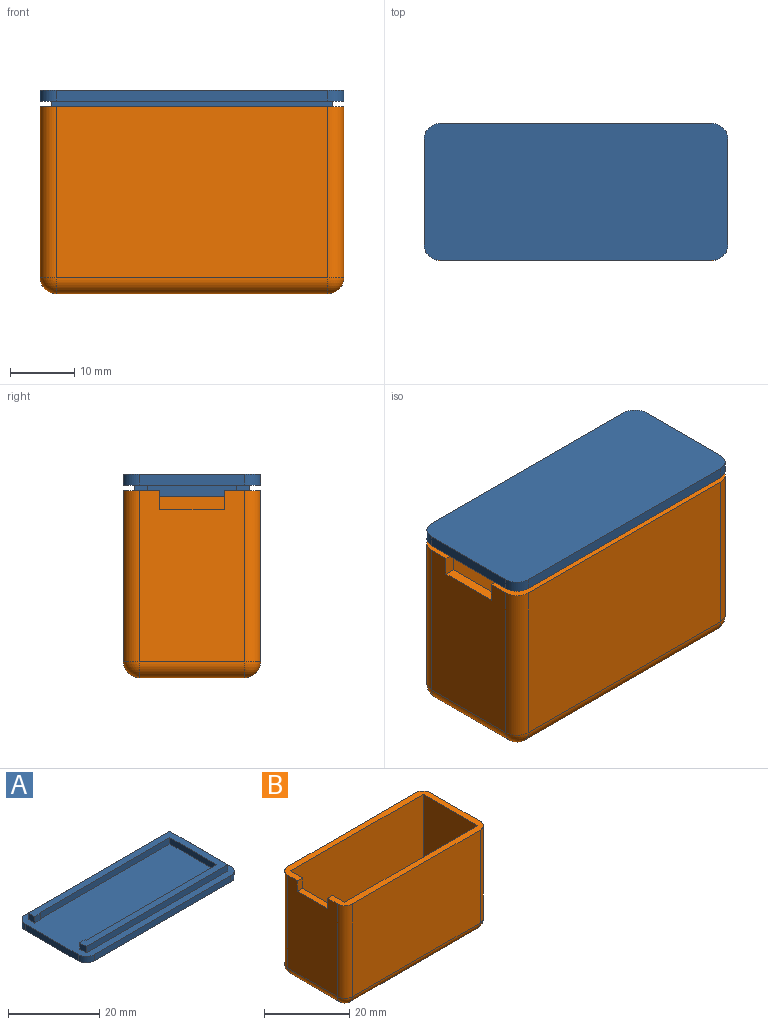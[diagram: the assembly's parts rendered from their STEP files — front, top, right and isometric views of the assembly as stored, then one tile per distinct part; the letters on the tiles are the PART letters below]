
ASSEMBLY  parts=2 mates=1
PART A: 23 faces, bbox 47.4x21.4x3.4 mm
  f0: plane 2x1.7mm, normal (-1,0,0), area 3.4mm2, adj f2,f7,f10,f18
  f1: plane 1.7x0.3mm, normal (1,0,0), area 0.5mm2, adj f2,f7,f14,f17
  f2: plane 44x18mm, normal (0,0,1), area 175.4mm2, adj f0,f1,f9,f10,f11,f12,f13,f14
  f3: plane 42.4x1.7mm, normal (0,1,0), area 72.1mm2, adj f7,f8,f19,f22
  f4: plane 16.4x1.7mm, normal (-1,0,0), area 27.9mm2, adj f7,f8,f19,f20
  f5: plane 42.4x1.7mm, normal (0,-1,0), area 72.1mm2, adj f7,f8,f20,f21
  f6: plane 16.4x1.7mm, normal (1,0,0), area 27.9mm2, adj f7,f8,f21,f22
  f7: plane 47.4x21.4mm, normal (0,0,1), area 833.6mm2, adj f0,f1,f3,f4,f5,f6,f9,f10
  f8: plane 47.4x21.4mm, normal (0,0,-1), area 1009mm2, adj f3,f4,f5,f6,f19,f20,f21,f22
  f9: plane 18x1.7mm, normal (1,0,0), area 30.6mm2, adj f2,f7,f10,f16
  f10: plane 44x1.7mm, normal (0,1,0), area 74.8mm2, adj f0,f2,f7,f9
  f11: plane 2x1.7mm, normal (-1,0,0), area 3.4mm2, adj f2,f7,f16,f17
  f12: plane 40.6x1.7mm, normal (0,-1,0), area 69mm2, adj f2,f7,f13,f15
  f13: plane 14.6x1.7mm, normal (-1,0,0), area 24.8mm2, adj f2,f7,f12,f14
  f14: plane 40.6x1.7mm, normal (0,1,0), area 69mm2, adj f1,f2,f7,f13
  f15: plane 1.7x0.3mm, normal (1,0,0), area 0.5mm2, adj f2,f7,f12,f18
  f16: plane 44x1.7mm, normal (0,-1,0), area 74.8mm2, adj f2,f7,f9,f11
  f17: plane 1.7x1.7mm, normal (0,1,0), area 2.9mm2, adj f1,f2,f7,f11
  f18: plane 1.7x1.7mm, normal (0,-1,0), area 2.9mm2, adj f0,f2,f7,f15
  f19: cylinder r=2.5mm len=2.5mm, axis (0,0,1), area 6.7mm2, adj f3,f4,f7,f8
  f20: cylinder r=2.5mm len=2.5mm, axis (0,0,-1), area 6.7mm2, adj f4,f5,f7,f8
  f21: cylinder r=2.5mm len=2.5mm, axis (0,0,1), area 6.7mm2, adj f5,f6,f7,f8
  f22: cylinder r=2.5mm len=2.5mm, axis (0,0,-1), area 6.7mm2, adj f3,f6,f7,f8
PART B: 29 faces, bbox 47.4x21.4x29.2 mm
  f0: plane 47.4x21.4mm, normal (0,0,1), area 200mm2, adj f1,f2,f3,f4,f6,f7,f8,f9
  f1: plane 26.7x16.4mm, normal (-1,0,0), area 407.9mm2, adj f0,f14,f15,f16,f22,f26,f28
  f2: plane 42.4x26.7mm, normal (0,-1,0), area 1132.1mm2, adj f0,f19,f25,f28
  f3: plane 26.7x16.4mm, normal (1,0,0), area 406.8mm2, adj f0,f11,f12,f13,f17,f19,f20
  f4: plane 42.4x26.7mm, normal (0,1,0), area 1132.1mm2, adj f0,f17,f21,f22
  f5: plane 42.4x16.4mm, normal (0,0,-1), area 695.4mm2, adj f20,f21,f25,f26
  f6: plane 27.5x18mm, normal (1,0,0), area 465mm2, adj f0,f7,f9,f10,f14,f15,f16
  f7: plane 44x27.5mm, normal (0,1,0), area 1210mm2, adj f0,f6,f8,f10
  f8: plane 27.5x18mm, normal (-1,0,0), area 457.2mm2, adj f0,f7,f9,f10,f11,f12,f13
  f9: plane 44x27.5mm, normal (0,-1,0), area 1210mm2, adj f0,f6,f8,f10
  f10: plane 45.57x18mm, normal (0,0,1), area 805.2mm2, adj f6,f7,f8,f9,f11,f12,f20
  f11: plane 4.5x1.7mm, normal (0,1,0), area 7.6mm2, adj f3,f8,f10,f13,f20
  f12: plane 4.5x1.7mm, normal (0,-1,0), area 7.6mm2, adj f3,f8,f10,f13,f20
  f13: plane 8.4x1.7mm, normal (0,0,-1), area 14.3mm2, adj f3,f8,f11,f12
  f14: plane 10x1.7mm, normal (0,0,1), area 17mm2, adj f1,f6,f15,f16
  f15: plane 3x1.7mm, normal (0,1,0), area 5.1mm2, adj f0,f1,f6,f14
  f16: plane 3x1.7mm, normal (0,-1,0), area 5.1mm2, adj f0,f1,f6,f14
  f17: cylinder r=2.5mm len=26.7mm, axis (0,0,1), area 104.9mm2, adj f0,f3,f4,f18
  f18: sphere r=2.5mm, area 9.8mm2, adj f17,f20,f21
  f19: cylinder r=2.5mm len=26.7mm, axis (0,0,-1), area 104.9mm2, adj f0,f2,f3,f23
  f20: cylinder r=2.5mm len=16.4mm, axis (0,1,0), area 57.6mm2, adj f3,f5,f10,f11,f12,f18,f23
  f21: cylinder r=2.5mm len=42.4mm, axis (-1,0,0), area 166.5mm2, adj f4,f5,f18,f24
  f22: cylinder r=2.5mm len=26.7mm, axis (0,0,-1), area 104.9mm2, adj f0,f1,f4,f24
  f23: sphere r=2.5mm, area 9.8mm2, adj f19,f20,f25
  f24: sphere r=2.5mm, area 9.8mm2, adj f21,f22,f26
  f25: cylinder r=2.5mm len=42.4mm, axis (1,0,0), area 166.5mm2, adj f2,f5,f23,f27
  f26: cylinder r=2.5mm len=16.4mm, axis (0,-1,0), area 64.4mm2, adj f1,f5,f24,f27
  f27: sphere r=2.5mm, area 9.8mm2, adj f25,f26,f28
  f28: cylinder r=2.5mm len=26.7mm, axis (0,0,1), area 104.9mm2, adj f0,f1,f2,f27
PLACE A rot(axis=(1,0,0),180deg) t=(-16.95,-6.04,21.71)mm
PLACE B t=(-16.95,17.94,-8.34)mm fixed
MATE slider A.f2 <-> B.f0  axis (0,0,-1) through (27.05,17.94,18.31)mm
